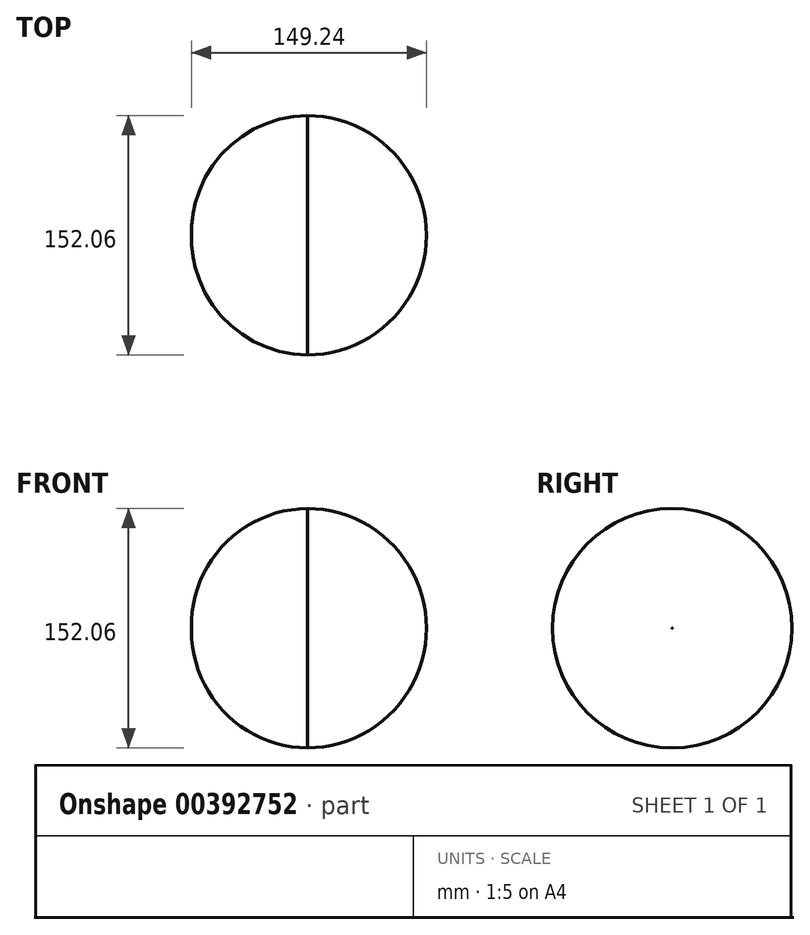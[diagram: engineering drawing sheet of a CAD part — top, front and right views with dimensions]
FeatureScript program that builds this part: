
annotation { "Feature Type Name" : "Feature", "Feature Type Description" : "" }
export const myFeature = defineFeature(function(context is Context, id is Id, definition is map)
    precondition{}
    {
        {
            var Q0;
            Q0=qCreatedBy(makeId("Front.planeOp"),FACE);
            var sketch = newSketch(context, id + "F0", { "sketchPlane" : qUnion([Q0])});
            skArc(sketch, "E0", {"start": v(0, 76.03) * mm, "mid": v(-53.93, 53.86) * mm, "end": v(-76.27, 0) * mm});
            skArc(sketch, "E1", {"start": v(74.8, 0) * mm, "mid": v(53.52, 53.87) * mm, "end": v(0, 76.03) * mm});
            skLineSegment(sketch, "E2", {"start": v(-76.27, 0) * mm, "end": v(74.8, 0) * mm});
            skSolve(sketch);
        }
        {
            var Q0;
            Q0 = qSketchRegion(id + "F0", true);
            var Q1;
            Q1=sQuery(id+"F0.wireOp",EDGE,"E2");
            revolve(context, id + "F1", {"entities" : qUnion([Q0]), "axis" : qUnion([Q1]), "revolveType" : RevolveType.FULL});
        }
    });
